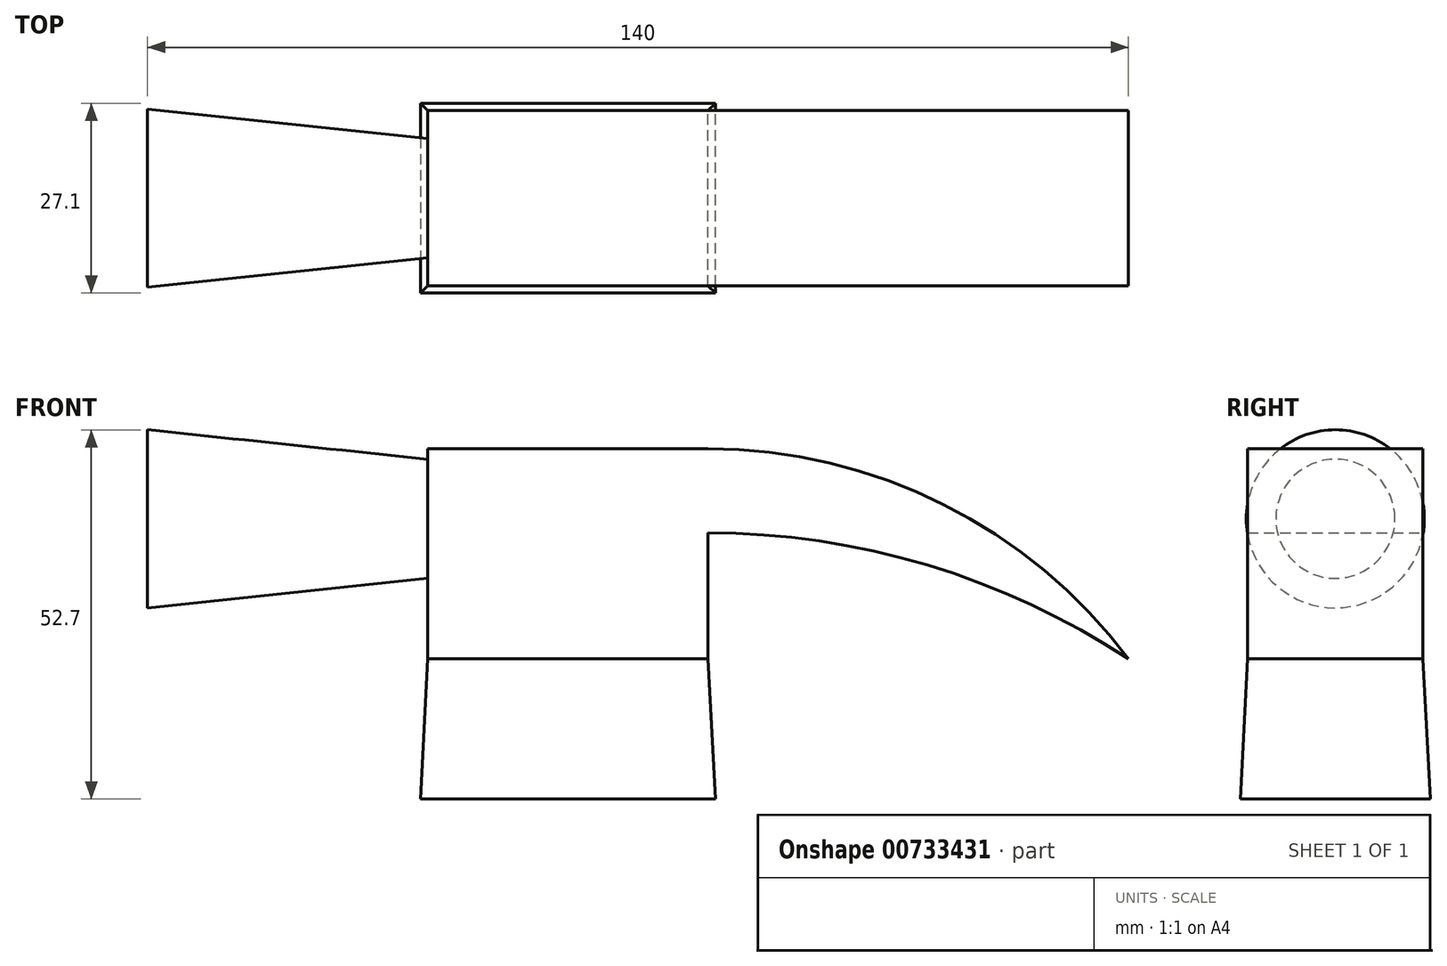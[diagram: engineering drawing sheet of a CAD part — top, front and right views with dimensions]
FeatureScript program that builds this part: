
annotation { "Feature Type Name" : "Feature", "Feature Type Description" : "" }
export const myFeature = defineFeature(function(context is Context, id is Id, definition is map)
    precondition{}
    {
        {
            var Q0;
            Q0=qCreatedBy(makeId("Front.planeOp"),FACE);
            var sketch = newSketch(context, id + "F0", { "sketchPlane" : qUnion([Q0])});
            skLineSegment(sketch, "E0.0", {"start": v(-20, 0) * mm, "end": v(-20, 30) * mm});
            skLineSegment(sketch, "E1.0", {"start": v(20, 0) * mm, "end": v(20, 30) * mm});
            skLineSegment(sketch, "E2", {"start": v(-20, 0) * mm, "end": v(20, 0) * mm});
            skLineSegment(sketch, "E3.0", {"start": v(-20, 30) * mm, "end": v(20, 30) * mm});
            skSolve(sketch);
        }
        {
            var Q0;
            Q0=qSketchRegion(id+"F0",true);
            extrude(context, id + "F1", {"entities" : qUnion([Q0]), "endBound" : BoundingType.SYMMETRIC, "depth" : 25 * mm, "offsetDistance" : 25 * mm});
        }
        {
            var Q0;
            Q0=makeQuery(id+"F1.opExtrude","SWEPT_FACE",FACE,{"disambiguationData":[OSD([sQuery(id+"F0.wireOp",EDGE,"E0.0")])]});
            var sketch = newSketch(context, id + "F2", { "sketchPlane" : qUnion([Q0])});
            skCircle(sketch, "E4", {"center": v(0, 20) * mm, "radius": 8.5 * mm});
            skSolve(sketch);
        }
        {
            var Q0;
            Q0=qSketchRegion(id+"F2",true);
            extrude(context, id + "F3", {"entities" : qUnion([Q0]), "operationType" : NewBodyOperationType.ADD, "depth" : 40 * mm, "offsetDistance" : 25 * mm, "hasDraft" : true, "draftAngle" : 6 * degree});
        }
        {
            var Q0;
            Q0=qCreatedBy(makeId("Front.planeOp"),FACE);
            var sketch = newSketch(context, id + "F4", { "sketchPlane" : qUnion([Q0])});
            skArc(sketch, "E5", {"start": v(80, 0) * mm, "mid": v(53.54, 22.08) * mm, "end": v(20, 30) * mm});
            skArc(sketch, "E6", {"start": v(80, 0) * mm, "mid": v(51.32, 13.4) * mm, "end": v(20, 18) * mm});
            skLineSegment(sketch, "E7", {"start": v(20, 30) * mm, "end": v(20, 18) * mm});
            skSolve(sketch);
        }
        {
            var Q0;
            Q0=qSketchRegion(id+"F4",true);
            extrude(context, id + "F5", {"entities" : qUnion([Q0]), "operationType" : NewBodyOperationType.ADD, "endBound" : BoundingType.SYMMETRIC, "depth" : 25 * mm, "offsetDistance" : 25 * mm});
        }
        {
            var Q0;
            Q0=makeQuery(id+"F1.opExtrude","SWEPT_FACE",FACE,{"disambiguationData":[OSD([sQuery(id+"F0.wireOp",EDGE,"E2")])]});
            extrude(context, id + "F6", {"entities" : qUnion([Q0]), "depth" : 20 * mm, "offsetDistance" : 25 * mm, "hasDraft" : true, "draftAngle" : 3 * degree});
        }
    });
